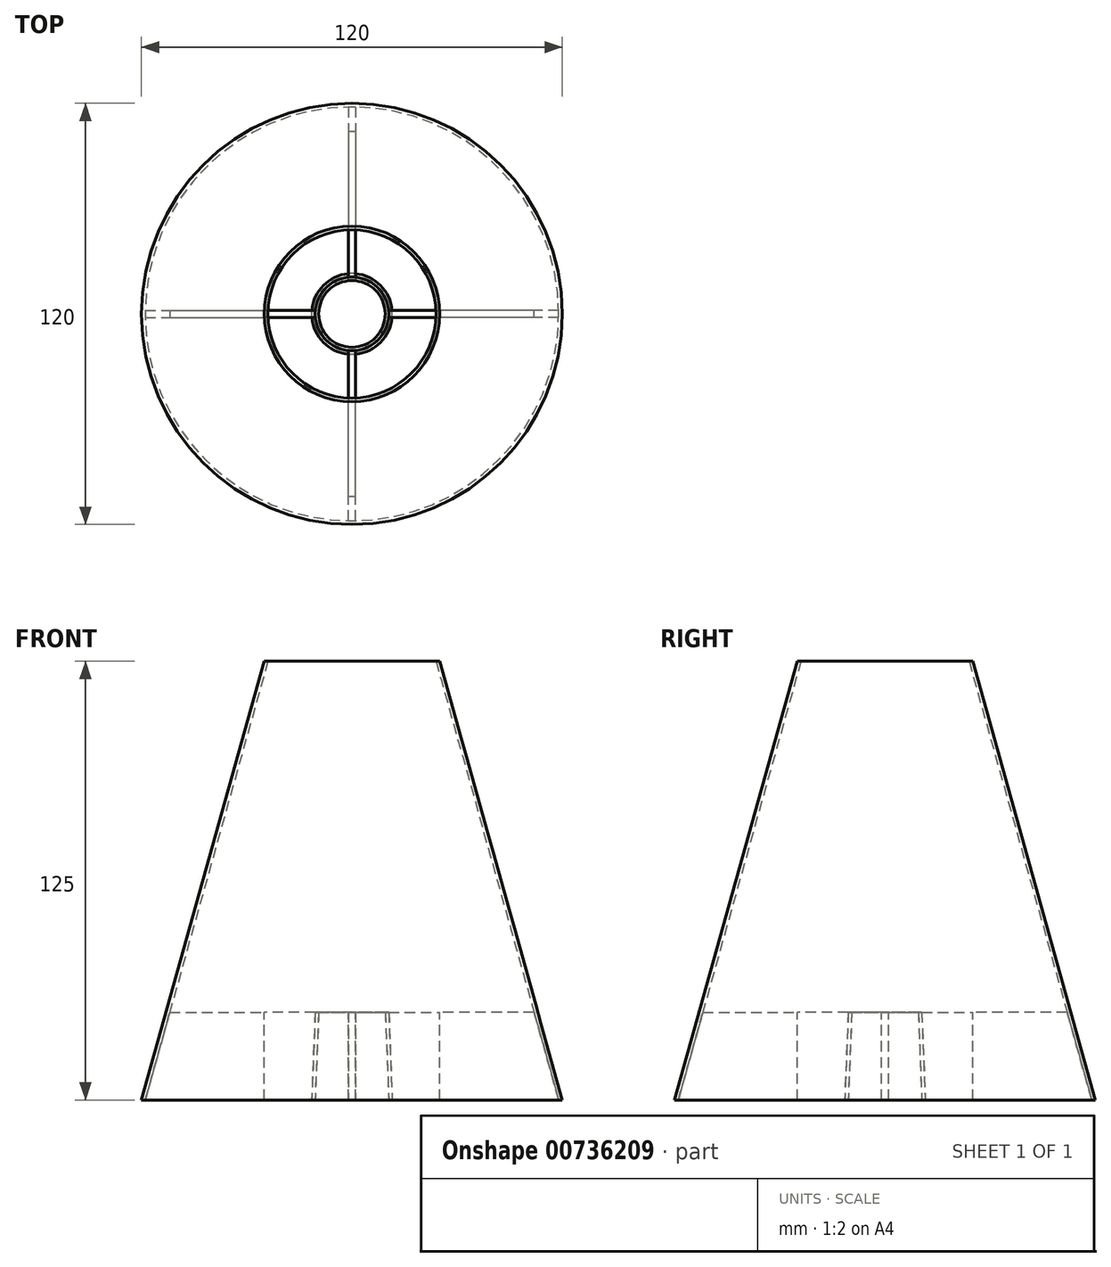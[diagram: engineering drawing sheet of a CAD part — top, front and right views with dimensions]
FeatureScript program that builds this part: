
annotation { "Feature Type Name" : "Feature", "Feature Type Description" : "" }
export const myFeature = defineFeature(function(context is Context, id is Id, definition is map)
    precondition{}
    {
        {
            var Q0;
            Q0=qCreatedBy(makeId("Top.planeOp"),FACE);
            var sketch = newSketch(context, id + "F0", { "sketchPlane" : qUnion([Q0])});
            skCircle(sketch, "E0", {"center": v(0, 0) * mm, "radius": 60 * mm});
            skSolve(sketch);
        }
        {
            var Q0;
            Q0=qCreatedBy(makeId("Top.planeOp"),FACE);
            cPlane(context, id + "F1", {"entities" : qUnion([Q0]), "cplaneType" : CPlaneType.OFFSET, "offset" : 125 * mm, "width" : 150 * mm, "height" : 150 * mm});
        }
        {
            var Q0;
            Q0=qCreatedBy(id+"F1.planeOp",FACE);
            var sketch = newSketch(context, id + "F2", { "sketchPlane" : qUnion([Q0])});
            skCircle(sketch, "E1", {"center": v(0, 0) * mm, "radius": 25 * mm});
            skSolve(sketch);
        }
        {
            var Q0;
            Q0=makeQuery(id+"F2.imprint","IMPRINT",FACE,{"disambiguationData":[TD([[makeQuery(id+"F2.imprint","IMPRINT",EDGE,{"derivedFrom":sQuery(id+"F2.wireOp",EDGE,"E1")}),1.0]])]});
            var Q1;
            Q1=makeQuery(id+"F0.imprint","IMPRINT",FACE,{"disambiguationData":[TD([[makeQuery(id+"F0.imprint","IMPRINT",EDGE,{"derivedFrom":sQuery(id+"F0.wireOp",EDGE,"E0")}),1.0]])]});
            loft(context, id + "F3", {"sheetProfilesArray" : [{ "sheetProfileEntities" : qUnion([Q0]) }, { "sheetProfileEntities" : qUnion([Q1]) }]});
        }
        {
            var Q0;
            Q0=makeQuery(id+"F3.opLoft","CAP_FACE",FACE,{"disambiguationData":[OSD([makeQuery(id+"F0.imprint","IMPRINT",FACE,{"disambiguationData":[TD([[makeQuery(id+"F0.imprint","IMPRINT",EDGE,{"derivedFrom":sQuery(id+"F0.wireOp",EDGE,"E0")}),1.0]])]})])],"isStart":true});
            var Q1;
            Q1=makeQuery(id+"F3.opLoft","CAP_FACE",FACE,{"disambiguationData":[OSD([makeQuery(id+"F2.imprint","IMPRINT",FACE,{"disambiguationData":[TD([[makeQuery(id+"F2.imprint","IMPRINT",EDGE,{"derivedFrom":sQuery(id+"F2.wireOp",EDGE,"E1")}),1.0]])]})])],"isStart":true});
            shell(context, id + "F4", {"entities" : qUnion([Q0, Q1]), "thickness" : 1 * mm});
        }
        {
            var Q0;
            Q0=qCreatedBy(makeId("Top.planeOp"),FACE);
            var sketch = newSketch(context, id + "F5", { "sketchPlane" : qUnion([Q0])});
            skCircle(sketch, "E2", {"center": v(0, 0) * mm, "radius": 11.5 * mm});
            skSolve(sketch);
        }
        {
            var Q0;
            Q0=qCreatedBy(makeId("Top.planeOp"),FACE);
            cPlane(context, id + "F6", {"entities" : qUnion([Q0]), "cplaneType" : CPlaneType.OFFSET, "offset" : 25 * mm, "width" : 150 * mm, "height" : 150 * mm});
        }
        {
            var Q0;
            Q0=qCreatedBy(id+"F6.planeOp",FACE);
            var sketch = newSketch(context, id + "F7", { "sketchPlane" : qUnion([Q0])});
            skCircle(sketch, "E3", {"center": v(0, 0) * mm, "radius": 10.5 * mm});
            skSolve(sketch);
        }
        {
            var Q0;
            Q0 = qSketchRegion(id + "F7", true);
            var Q1;
            Q1=makeQuery(id+"F5.imprint","IMPRINT",FACE,{"disambiguationData":[TD([[makeQuery(id+"F5.imprint","IMPRINT",EDGE,{"derivedFrom":sQuery(id+"F5.wireOp",EDGE,"E2")}),1.0]])]});
            loft(context, id + "F8", {"sheetProfilesArray" : [{ "sheetProfileEntities" : qUnion([Q0]) }, { "sheetProfileEntities" : qUnion([Q1]) }]});
        }
        {
            var Q0;
            Q0=makeQuery(id+"F8.opLoft","CAP_FACE",FACE,{"disambiguationData":[OSD([makeQuery(id+"F5.imprint","IMPRINT",FACE,{"disambiguationData":[TD([[makeQuery(id+"F5.imprint","IMPRINT",EDGE,{"derivedFrom":sQuery(id+"F5.wireOp",EDGE,"E2")}),1.0]])]})])],"isStart":true});
            var Q1;
            Q1=makeQuery(id+"F8.opLoft","CAP_FACE",FACE,{"disambiguationData":[OSD([makeQuery(id+"F7.imprint","IMPRINT",FACE,{"disambiguationData":[TD([[makeQuery(id+"F7.imprint","IMPRINT",EDGE,{"derivedFrom":sQuery(id+"F7.wireOp",EDGE,"E3")}),1.0]])]})])],"isStart":true});
            shell(context, id + "F9", {"entities" : qUnion([Q0, Q1]), "thickness" : 1 * mm});
        }
        {
            var Q0;
            Q0=qCreatedBy(makeId("Right.planeOp"),FACE);
            cPlane(context, id + "F10", {"entities" : qUnion([Q0]), "cplaneType" : CPlaneType.OFFSET, "offset" : 25 * mm, "oppositeDirection" : true, "width" : 150 * mm, "height" : 150 * mm});
        }
        {
            var Q0;
            Q0=qCreatedBy(id+"F10.planeOp",FACE);
            var sketch = newSketch(context, id + "F11", { "sketchPlane" : qUnion([Q0])});
            skLineSegment(sketch, "E4.bottom", {"start": v(1, 0) * mm, "end": v(-1, 0) * mm});
            skLineSegment(sketch, "E4.top", {"start": v(1, 25) * mm, "end": v(-1, 25) * mm});
            skLineSegment(sketch, "E4.left", {"start": v(1, 0) * mm, "end": v(1, 25) * mm});
            skLineSegment(sketch, "E4.right", {"start": v(-1, 0) * mm, "end": v(-1, 25) * mm});
            skSolve(sketch);
        }
        {
            var Q0;
            Q0 = qSketchRegion(id + "F11", true);
            extrude(context, id + "F12", {"entities" : qUnion([Q0]), "operationType" : NewBodyOperationType.ADD, "endBound" : BoundingType.UP_TO_NEXT, "depth" : 25 * mm, "offsetDistance" : 25 * mm});
        }
        {
            var Q0;
            Q0 = qSketchRegion(id + "F11", true);
            extrude(context, id + "F13", {"entities" : qUnion([Q0]), "endBound" : BoundingType.UP_TO_NEXT, "oppositeDirection" : true, "depth" : 25 * mm, "offsetDistance" : 25 * mm});
        }
        {
            var Q0;
            Q0=makeQuery(id+"F13.opExtrude","SWEPT_BODY",BODY,{"disambiguationData":[OSD([sQuery(id+"F11.wireOp",EDGE,"E4.bottom"),sQuery(id+"F11.wireOp",EDGE,"E4.top"),sQuery(id+"F11.wireOp",EDGE,"E4.left"),sQuery(id+"F11.wireOp",EDGE,"E4.right")])]});
            var Q1;
            Q1=makeQuery(id+"F8.opLoft","SWEPT_BODY",BODY,{"disambiguationData":[OSD([makeQuery(id+"F5.imprint","IMPRINT",FACE,{"disambiguationData":[TD([[makeQuery(id+"F5.imprint","IMPRINT",EDGE,{"derivedFrom":sQuery(id+"F5.wireOp",EDGE,"E2")}),1.0]])]}),makeQuery(id+"F7.imprint","IMPRINT",FACE,{"disambiguationData":[TD([[makeQuery(id+"F7.imprint","IMPRINT",EDGE,{"derivedFrom":sQuery(id+"F7.wireOp",EDGE,"E3")}),1.0]])]})])]});
            var Q2;
            Q2=makeQuery(id+"F9.opShell","OFFSET_FACE",FACE,{"disambiguationData":[OSD([sQuery(id+"F5.wireOp",EDGE,"E2"),sQuery(id+"F7.wireOp",EDGE,"E3")])]});
            circularPattern(context, id + "F14", {"entities" : qUnion([Q0, Q1]), "axis" : qUnion([Q2]), "angle" : 360 * degree, "instanceCount" : 4, "equalSpace" : true});
        }
    });
